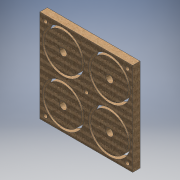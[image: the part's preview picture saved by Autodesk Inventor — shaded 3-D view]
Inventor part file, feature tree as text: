
AUTODESK INVENTOR PART (.ipt)
format: ipt  version: 2016 (Build 200138000, 138)  size: 200,704 bytes
history: native  units: mm
features: extrude x1, sketch x1
ambient origin geometry x8: Origin, YZ Plane, XZ Plane, XY Plane, X Axis, Y Axis, Z Axis, Center Point
bodies: Solid1 (feature_tree)
feature tree (2):
  extrude  "Extrusion1"  Depth=80.0mm
  sketch  "Sketch1"  dims[d0=80.0mm d1=80.0mm d2=36.2235mm d3=2.0mm d4=6.3mm d5=3.43mm d6=50.0mm d7=3.43mm d8=6.39mm d9=0.0mm]
